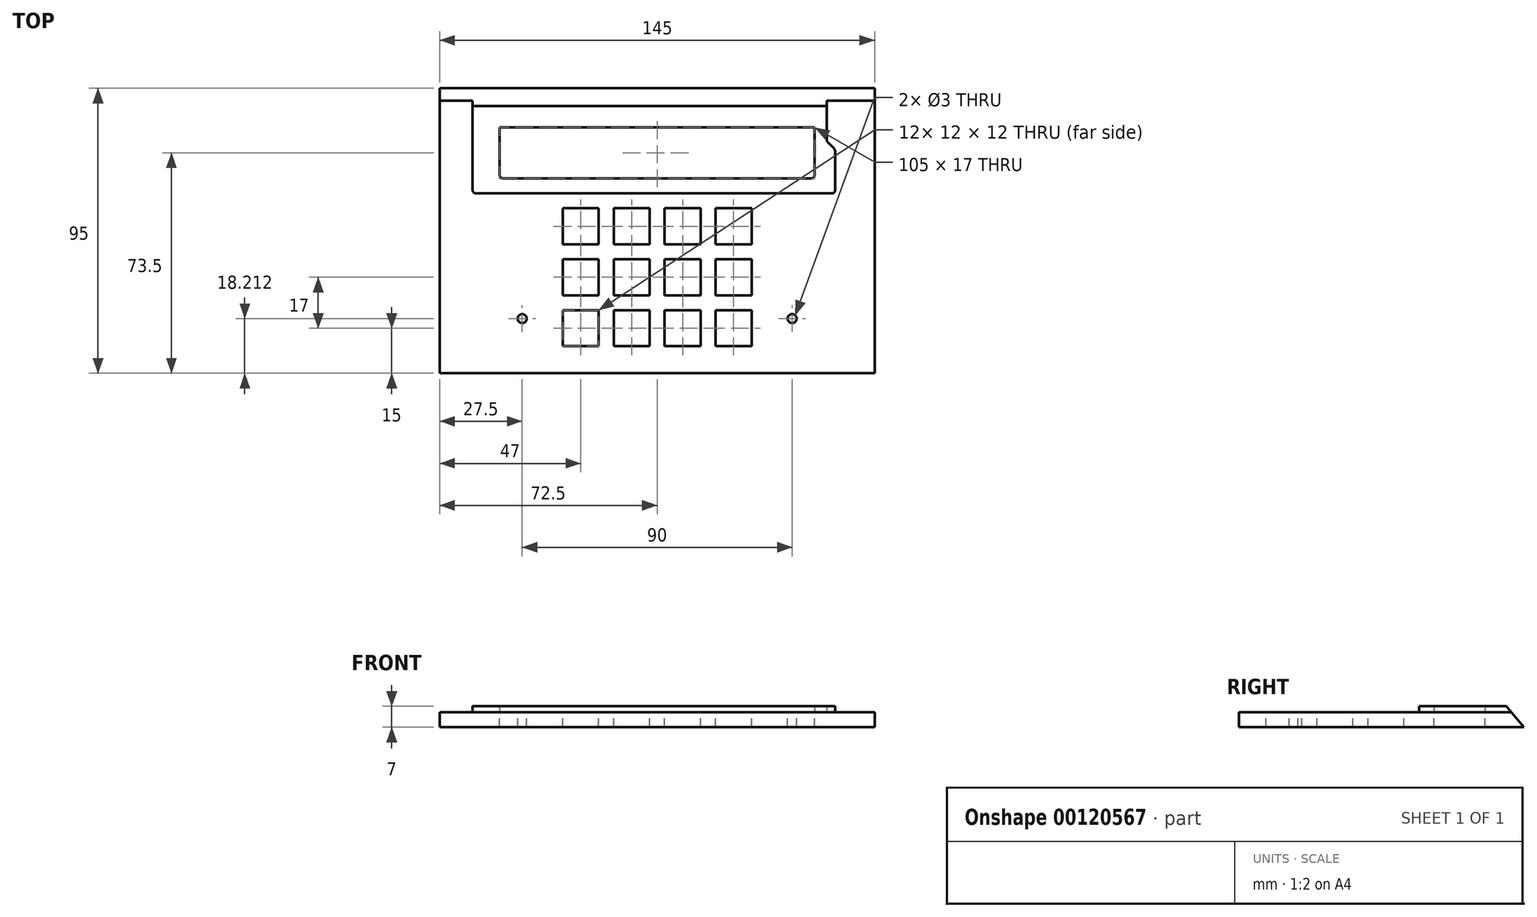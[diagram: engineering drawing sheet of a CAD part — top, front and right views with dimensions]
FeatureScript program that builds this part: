
annotation { "Feature Type Name" : "Feature", "Feature Type Description" : "" }
export const myFeature = defineFeature(function(context is Context, id is Id, definition is map)
    precondition{}
    {
        {
            var Q0;
            Q0=qCreatedBy(makeId("Top.planeOp"),FACE);
            var sketch = newSketch(context, id + "F0", { "sketchPlane" : qUnion([Q0])});
            skLineSegment(sketch, "E0.bottom", {"start": v(0, 0) * mm, "end": v(145, 0) * mm});
            skLineSegment(sketch, "E0.left", {"start": v(0, 0) * mm, "end": v(0, -95) * mm});
            skLineSegment(sketch, "E0.right", {"start": v(145, 0) * mm, "end": v(145, -95) * mm});
            skLineSegment(sketch, "E1.bottom", {"start": v(20, -13) * mm, "end": v(125, -13) * mm});
            skLineSegment(sketch, "E1.top", {"start": v(20, -30) * mm, "end": v(125, -30) * mm});
            skLineSegment(sketch, "E1.left", {"start": v(20, -13) * mm, "end": v(20, -30) * mm});
            skLineSegment(sketch, "E1.right", {"start": v(125, -13) * mm, "end": v(125, -30) * mm});
            skLineSegment(sketch, "E2.bottom", {"start": v(58, -40) * mm, "end": v(70, -40) * mm});
            skLineSegment(sketch, "E2.top", {"start": v(58, -52) * mm, "end": v(70, -52) * mm});
            skLineSegment(sketch, "E2.left", {"start": v(58, -40) * mm, "end": v(58, -52) * mm});
            skLineSegment(sketch, "E2.right", {"start": v(70, -40) * mm, "end": v(70, -52) * mm});
            skLineSegment(sketch, "E3.bottom", {"start": v(75, -40) * mm, "end": v(87, -40) * mm});
            skLineSegment(sketch, "E3.top", {"start": v(75, -52) * mm, "end": v(87, -52) * mm});
            skLineSegment(sketch, "E3.left", {"start": v(75, -40) * mm, "end": v(75, -52) * mm});
            skLineSegment(sketch, "E3.right", {"start": v(87, -40) * mm, "end": v(87, -52) * mm});
            skLineSegment(sketch, "E4.bottom", {"start": v(41, -40) * mm, "end": v(53, -40) * mm});
            skLineSegment(sketch, "E4.top", {"start": v(41, -52) * mm, "end": v(53, -52) * mm});
            skLineSegment(sketch, "E4.left", {"start": v(41, -40) * mm, "end": v(41, -52) * mm});
            skLineSegment(sketch, "E4.right", {"start": v(53, -40) * mm, "end": v(53, -52) * mm});
            skLineSegment(sketch, "E5.bottom", {"start": v(41, -57) * mm, "end": v(53, -57) * mm});
            skLineSegment(sketch, "E5.top", {"start": v(41, -69) * mm, "end": v(53, -69) * mm});
            skLineSegment(sketch, "E5.left", {"start": v(41, -57) * mm, "end": v(41, -69) * mm});
            skLineSegment(sketch, "E5.right", {"start": v(53, -57) * mm, "end": v(53, -69) * mm});
            skLineSegment(sketch, "E6.bottom", {"start": v(58, -57) * mm, "end": v(70, -57) * mm});
            skLineSegment(sketch, "E6.top", {"start": v(58, -69) * mm, "end": v(70, -69) * mm});
            skLineSegment(sketch, "E6.left", {"start": v(58, -57) * mm, "end": v(58, -69) * mm});
            skLineSegment(sketch, "E6.right", {"start": v(70, -57) * mm, "end": v(70, -69) * mm});
            skLineSegment(sketch, "E7", {"start": v(0, -95) * mm, "end": v(145, -95) * mm});
            skLineSegment(sketch, "E8", {"start": v(75, -57) * mm, "end": v(75, -69) * mm});
            skLineSegment(sketch, "E9", {"start": v(75, -69) * mm, "end": v(87, -69) * mm});
            skLineSegment(sketch, "E10", {"start": v(87, -69) * mm, "end": v(87, -57) * mm});
            skLineSegment(sketch, "E11", {"start": v(87, -57) * mm, "end": v(75, -57) * mm});
            skLineSegment(sketch, "E12.bottom", {"start": v(92, -57) * mm, "end": v(104, -57) * mm});
            skLineSegment(sketch, "E12.top", {"start": v(92, -69) * mm, "end": v(104, -69) * mm});
            skLineSegment(sketch, "E12.left", {"start": v(92, -57) * mm, "end": v(92, -69) * mm});
            skLineSegment(sketch, "E12.right", {"start": v(104, -57) * mm, "end": v(104, -69) * mm});
            skLineSegment(sketch, "E13.bottom", {"start": v(92, -40) * mm, "end": v(104, -40) * mm});
            skLineSegment(sketch, "E13.top", {"start": v(92, -52) * mm, "end": v(104, -52) * mm});
            skLineSegment(sketch, "E13.left", {"start": v(92, -40) * mm, "end": v(92, -52) * mm});
            skLineSegment(sketch, "E13.right", {"start": v(104, -40) * mm, "end": v(104, -52) * mm});
            skLineSegment(sketch, "E14.bottom", {"start": v(75, -74) * mm, "end": v(87, -74) * mm});
            skLineSegment(sketch, "E14.top", {"start": v(75, -86) * mm, "end": v(87, -86) * mm});
            skLineSegment(sketch, "E14.left", {"start": v(75, -74) * mm, "end": v(75, -86) * mm});
            skLineSegment(sketch, "E14.right", {"start": v(87, -74) * mm, "end": v(87, -86) * mm});
            skLineSegment(sketch, "E15.bottom", {"start": v(92, -74) * mm, "end": v(104, -74) * mm});
            skLineSegment(sketch, "E15.top", {"start": v(92, -86) * mm, "end": v(104, -86) * mm});
            skLineSegment(sketch, "E15.left", {"start": v(92, -74) * mm, "end": v(92, -86) * mm});
            skLineSegment(sketch, "E15.right", {"start": v(104, -74) * mm, "end": v(104, -86) * mm});
            skLineSegment(sketch, "E16.bottom", {"start": v(58, -74) * mm, "end": v(70, -74) * mm});
            skLineSegment(sketch, "E16.top", {"start": v(58, -86) * mm, "end": v(70, -86) * mm});
            skLineSegment(sketch, "E16.left", {"start": v(58, -74) * mm, "end": v(58, -86) * mm});
            skLineSegment(sketch, "E16.right", {"start": v(70, -74) * mm, "end": v(70, -86) * mm});
            skLineSegment(sketch, "E17.bottom", {"start": v(41, -74) * mm, "end": v(53, -74) * mm});
            skLineSegment(sketch, "E17.top", {"start": v(41, -86) * mm, "end": v(53, -86) * mm});
            skLineSegment(sketch, "E17.left", {"start": v(41, -74) * mm, "end": v(41, -86) * mm});
            skLineSegment(sketch, "E17.right", {"start": v(53, -74) * mm, "end": v(53, -86) * mm});
            skCircle(sketch, "E18", {"center": v(27.5, -76.79) * mm, "radius": 8.5 * mm, "construction": true});
            skCircle(sketch, "E19", {"center": v(27.5, -76.79) * mm, "radius": 1.5 * mm});
            skCircle(sketch, "E20", {"center": v(117.5, -76.79) * mm, "radius": 8.5 * mm, "construction": true});
            skCircle(sketch, "E21", {"center": v(117.5, -76.79) * mm, "radius": 1.5 * mm});
            skSolve(sketch);
        }
        {
            var Q0;
            Q0=makeQuery(id+"F0.imprint","IMPRINT",FACE,{"disambiguationData":[TD([[makeQuery(id+"F0.imprint","IMPRINT",EDGE,{"derivedFrom":sQuery(id+"F0.wireOp",EDGE,"E0.bottom")}),-1.0]])]});
            extrude(context, id + "F1", {"entities" : qUnion([Q0]), "oppositeDirection" : true, "depth" : 5 * mm});
        }
        {
            var Q0;
            Q0=qCreatedBy(makeId("Top.planeOp"),FACE);
            var sketch = newSketch(context, id + "F2", { "sketchPlane" : qUnion([Q0])});
            skLineSegment(sketch, "E22.bottom", {"start": v(11, 0) * mm, "end": v(129, 0) * mm});
            skLineSegment(sketch, "E22.top", {"start": v(12, -35) * mm, "end": v(130.86, -35) * mm});
            skLineSegment(sketch, "E22.left", {"start": v(11, 0) * mm, "end": v(11, -34) * mm});
            skLineSegment(sketch, "E22.right", {"start": v(131.86, -21.26) * mm, "end": v(131.86, -34) * mm});
            skLineSegment(sketch, "E23.bottom", {"start": v(20, -13) * mm, "end": v(125, -13) * mm});
            skLineSegment(sketch, "E23.top", {"start": v(21, -30) * mm, "end": v(124, -30) * mm});
            skLineSegment(sketch, "E23.left", {"start": v(20, -13) * mm, "end": v(20, -29) * mm});
            skLineSegment(sketch, "E23.right", {"start": v(125, -13) * mm, "end": v(125, -29) * mm});
            skLineSegment(sketch, "E24", {"start": v(129, 0) * mm, "end": v(129, -16.83) * mm});
            skLineSegment(sketch, "E25", {"start": v(129.63, -18.29) * mm, "end": v(131.24, -19.8) * mm});
            skPoint(sketch, "E26.visualSharp", {"position": v(129, -17.7) * mm});
            skArc(sketch, "E26.filletArc", {"start": v(129, -16.83) * mm, "mid": v(129.16, -17.62) * mm, "end": v(129.63, -18.29) * mm});
            skPoint(sketch, "E27.visualSharp", {"position": v(131.86, -20.4) * mm});
            skArc(sketch, "E27.filletArc", {"start": v(131.86, -21.26) * mm, "mid": v(131.7, -20.46) * mm, "end": v(131.24, -19.8) * mm});
            skPoint(sketch, "E28.visualSharp", {"position": v(20, -30) * mm});
            skArc(sketch, "E28.filletArc", {"start": v(20, -29) * mm, "mid": v(20.3, -29.7) * mm, "end": v(21, -30) * mm});
            skPoint(sketch, "E29.visualSharp", {"position": v(125, -30) * mm});
            skArc(sketch, "E29.filletArc", {"start": v(124, -30) * mm, "mid": v(124.7, -29.7) * mm, "end": v(125, -29) * mm});
            skPoint(sketch, "E30.visualSharp", {"position": v(11, -35) * mm});
            skArc(sketch, "E30.filletArc", {"start": v(11, -34) * mm, "mid": v(11.3, -34.7) * mm, "end": v(12, -35) * mm});
            skPoint(sketch, "E31.visualSharp", {"position": v(131.86, -35) * mm});
            skArc(sketch, "E31.filletArc", {"start": v(130.86, -35) * mm, "mid": v(131.57, -34.7) * mm, "end": v(131.86, -34) * mm});
            skSolve(sketch);
        }
        {
            var Q0;
            Q0 = qSketchRegion(id + "F2", true);
            extrude(context, id + "F3", {"entities" : qUnion([Q0]), "operationType" : NewBodyOperationType.ADD, "depth" : 2 * mm});
        }
        {
            var Q0;
            Q0=makeQuery(id+"F1.opExtrude","SWEPT_FACE",FACE,{"disambiguationData":[OSD([sQuery(id+"F0.wireOp",EDGE,"E0.left")])]});
            var sketch = newSketch(context, id + "F4", { "sketchPlane" : qUnion([Q0])});
            skLineSegment(sketch, "E32", {"start": v(0, -5) * mm, "end": v(8.4, 5) * mm});
            skLineSegment(sketch, "E33", {"start": v(8.4, 5) * mm, "end": v(0, 5) * mm});
            skLineSegment(sketch, "E34", {"start": v(0, 5) * mm, "end": v(0, -5) * mm});
            skSolve(sketch);
        }
        {
            var Q0;
            Q0 = qSketchRegion(id + "F4", true);
            extrude(context, id + "F5", {"entities" : qUnion([Q0]), "operationType" : NewBodyOperationType.REMOVE, "oppositeDirection" : true, "depth" : 200 * mm});
        }
    });
